# Revit family: Edelstahlrohrschelle V2A, M16, Ø169-280
name_source: partatom
category: HLS-Bauteile
revit_build: Autodesk Revit 2017 (Build: 20190507_1515(x64)
units: mm (PartAtom-declared; Revit-internal decimal feet)

## family parameters
Arbeitsebenenbasiert = Ja
Beim Laden mit Abzugskörper schneiden = Nein
Bemaßung runder Anschluss = Durchmesser verwenden
Gemeinsam genutzt = Ja
Immer vertikal = Nein
Raumberechnungspunkt = Nein
Teiletyp = Normal

## types (9) — shared parameters
A = 19 mm  [stored 0.062336 ft]
Anschluss = M16
Anschlußhöhe = 19 mm
Bauart = zweiteilig
DF1 = 29 mm  [stored 0.0951444 ft]
DF2 = 37 mm  [stored 0.121391 ft]
DVS = 11 mm  [stored 0.0360892 ft]
Fabrikat = MEFA
Firma = MEFA Befestigungs- und Montagesysteme GmbH
HGA = 15 mm  [stored 0.0492126 ft]
Kurztext1 = Rohrschelle Edelstahl V2A 35x4,0
MB = 35 mm  [stored 0.114829 ft]
MD = 4 mm  [stored 0.0131234 ft]
Material = Edelstahl
Materialmaße = 35x4,0 mm
Mengeneinheit = St
Verschluss = Schraubenverschluss
Verschluss-Schraube = M10
Vorgabe-Ansicht = 1219 mm
max. zul. Last horizontal = 0.00 kN
max. zul. Last vertikal = 0.00 kN
vpe = 1 St
zero-valued in all types: Nennweite DN Rohr, Rohraußendurchmesser, Stärke Material

## per-type parameters (varying)
| type | AB | Achsabstand | Artikelnummer | B | D | Dmax | Dmin | EAN | Gewicht | Gewicht pro Bauteil | H | Kurztext2 | R | RM | Rohraußendurchmesser Zoll | S | max. Rohraußendurchmesser | min. Rohraußendurchmesser |
| Edelstahlrohrschelle V2A, M16, Ø169-173 | 4 mm  [stored 0.0131234 ft] | 218 mm | 04634251 | 247 mm | 173 mm  [stored 0.567585 ft] | 173 mm  [stored 0.567585 ft] | 169 mm  [stored 0.554462 ft] | 4250928411525 | 0.82 kg | 0.82 kg | 196 mm  [stored 0.643045 ft] | 169 - 173 mm M16 | 87 mm | 91 mm | Zoll | 218 mm | 173 mm  [stored 0.567585 ft] | 169 mm  [stored 0.554462 ft] |
| Edelstahlrohrschelle V2A, M16, Ø174-178 | 4 mm  [stored 0.0131234 ft] | 223 mm | 04634252 | 252 mm | 178 mm  [stored 0.58399 ft] | 178 mm  [stored 0.58399 ft] | 174 mm  [stored 0.570866 ft] | 4250928411532 | 0.83 kg | 0.83 kg | 201 mm | 174 - 178 mm M16 | 89 mm  [stored 0.291995 ft] | 93 mm  [stored 0.305118 ft] | Zoll | 223 mm | 178 mm  [stored 0.58399 ft] | 174 mm  [stored 0.570866 ft] |
| Edelstahlrohrschelle V2A, M16, Ø193-200 | 7 mm  [stored 0.0229659 ft] | 245 mm | 0463428 | 274 mm | 200 mm  [stored 0.656168 ft] | 200 mm  [stored 0.656168 ft] | 193 mm  [stored 0.633202 ft] | 4250928411549 | 0.91 kg | 0.91 kg | 223 mm | 193 - 200 mm M16 | 100 mm  [stored 0.328084 ft] | 104 mm | Zoll | 245 mm | 200 mm  [stored 0.656168 ft] | 193 mm  [stored 0.633202 ft] |
| Edelstahlrohrschelle V2A, M16, Ø202-210 | 8 mm  [stored 0.0262467 ft] | 255 mm | 0463429 | 284 mm | 210 mm  [stored 0.688976 ft] | 210 mm  [stored 0.688976 ft] | 202 mm  [stored 0.66273 ft] | 4250928411556 | 0.93 kg | 0.93 kg | 233 mm | 202 - 210 mm M16 | 105 mm  [stored 0.344488 ft] | 109 mm  [stored 0.357612 ft] | Zoll | 255 mm | 210 mm  [stored 0.688976 ft] | 202 mm  [stored 0.66273 ft] |
| Edelstahlrohrschelle V2A, M16, Ø211-215 | 4 mm  [stored 0.0131234 ft] | 261 mm | 0463430 | 289 mm | 215 mm | 215 mm | 211 mm  [stored 0.692257 ft] | 4250928411563 | 0.96 kg | 0.96 kg | 238 mm | 211 - 215 mm M16 | 108 mm | 112 mm  [stored 0.367454 ft] | Zoll | 260 mm | 215 mm | 211 mm  [stored 0.692257 ft] |
| Edelstahlrohrschelle V2A, M16, Ø216-224 | 8 mm  [stored 0.0262467 ft] | 269 mm | 0463431 | 298 mm | 224 mm | 224 mm | 216 mm  [stored 0.708661 ft] | 4250928411570 | 0.97 kg | 0.97 kg | 247 mm | 216 - 224 mm M16 | 112 mm  [stored 0.367454 ft] | 116 mm  [stored 0.380577 ft] | 8 Zoll | 269 mm | 224 mm | 216 mm  [stored 0.708661 ft] |
| Edelstahlrohrschelle V2A, M16, Ø244-250 | 6 mm  [stored 0.019685 ft] | 295 mm | 0463434 | 324 mm | 250 mm | 250 mm | 244 mm | 4250928411587 | 1.07 kg | 1.07 kg | 273 mm | 244 - 250 mm M16 | 125 mm  [stored 0.410105 ft] | 129 mm  [stored 0.423228 ft] | Zoll | 295 mm | 250 mm | 244 mm |
| Edelstahlrohrschelle V2A, M16, Ø251-258 | 7 mm  [stored 0.0229659 ft] | 303 mm | 0463435 | 332 mm | 258 mm | 258 mm | 251 mm | 4250928411594 | 1.09 kg | 1.09 kg | 281 mm | 251 - 258 mm M16 | 129 mm  [stored 0.423228 ft] | 133 mm  [stored 0.436352 ft] | Zoll | 303 mm | 258 mm | 251 mm |
| Edelstahlrohrschelle,V2A, M16, Ø272-280 | 8 mm  [stored 0.0262467 ft] | 325 mm | 0463438 | 354 mm | 280 mm | 280 mm | 272 mm | 4250928411600 | 1.16 kg | 1.16 kg | 303 mm | 272 - 280 mm M16 | 140 mm  [stored 0.459318 ft] | 144 mm  [stored 0.472441 ft] | 10 Zoll | 325 mm | 280 mm | 272 mm |

note: [stored X ft] marks values corroborated as IEEE doubles in the binary element streams (Revit-internal decimal feet)

## geometry (parser evidence)
native form markers: Sweep x3
no freeform markers — native parametric forms only
